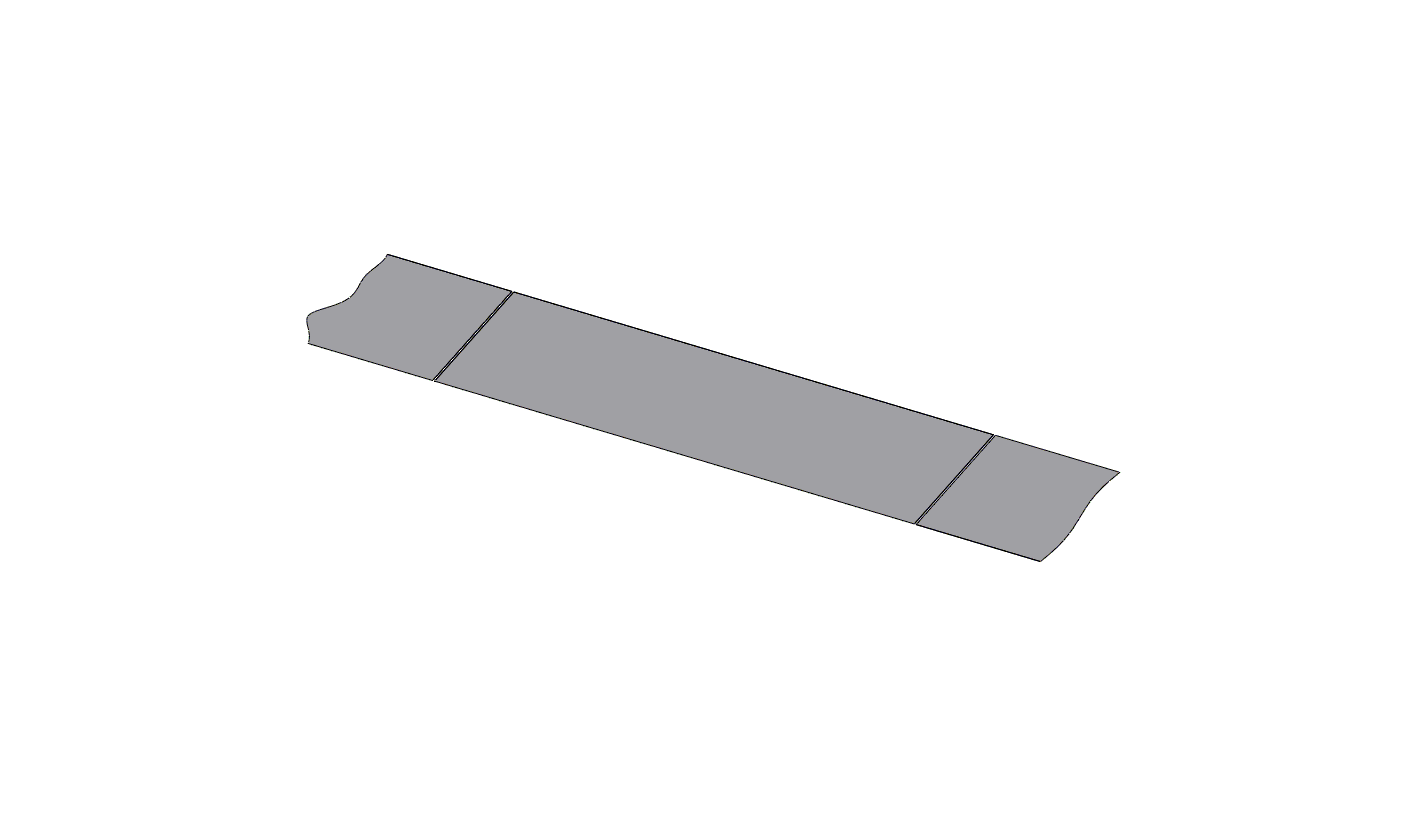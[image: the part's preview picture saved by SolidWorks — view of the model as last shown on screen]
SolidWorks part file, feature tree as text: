
SOLIDWORKS PART (.sldprt)
format: sldprt  version: not decoded by parser v0  size: 231,424 bytes
history: native  units: mm
features: sketch x13, material x1, sheet_metal_op x1, cut_extrude x1 + 5 further entries (+11 scaffold rows collapsed)
feature tree (32):
  scaffold x11  (default folders/planes/origin — collapsed)
  material  "AISI 1020 Steel, Cold Rolled"
  sheet_metal_op  "Sheet-Metal1"  Sheet-Metal2=0 Thickness=0.1mm Sheet-Metal3=0 Sheet-Metal4=0 Sheet-Metal5=0
  sketch  "Sharp-Sketch1"  dims[D1=0.0mm]
  sketch  "Flat-Sketch1"  dims[D1=0.0mm]
  sketch  "Sketch6"  dims[D1=1.0mm D2=250.0mm]
  cut_extrude  "Cut-Extrude1"  Depth=10mm
  "Flat-Pattern1"
  sketch  "Bend-Lines1"
  sketch  "Bounding-Box1"
  "Flat-Pattern2"
  sketch  "Bend-Lines2"
  sketch  "Bounding-Box2"
  "Flat-Pattern3"
  sketch  "Bend-Lines3"
  sketch  "Bounding-Box3"
  "Flat-Pattern4"
  sketch  "Bend-Lines4"
  sketch  "Bounding-Box4"
  "Flat-Pattern5"
  sketch  "Bend-Lines5"
  sketch  "Bounding-Box5"
decode coverage: 5 of 15 modeling features carry decoded parameters; 5 rows unclassified (native names shown)
note: suppression state not decoded; provenance and decode notes live in map.json
